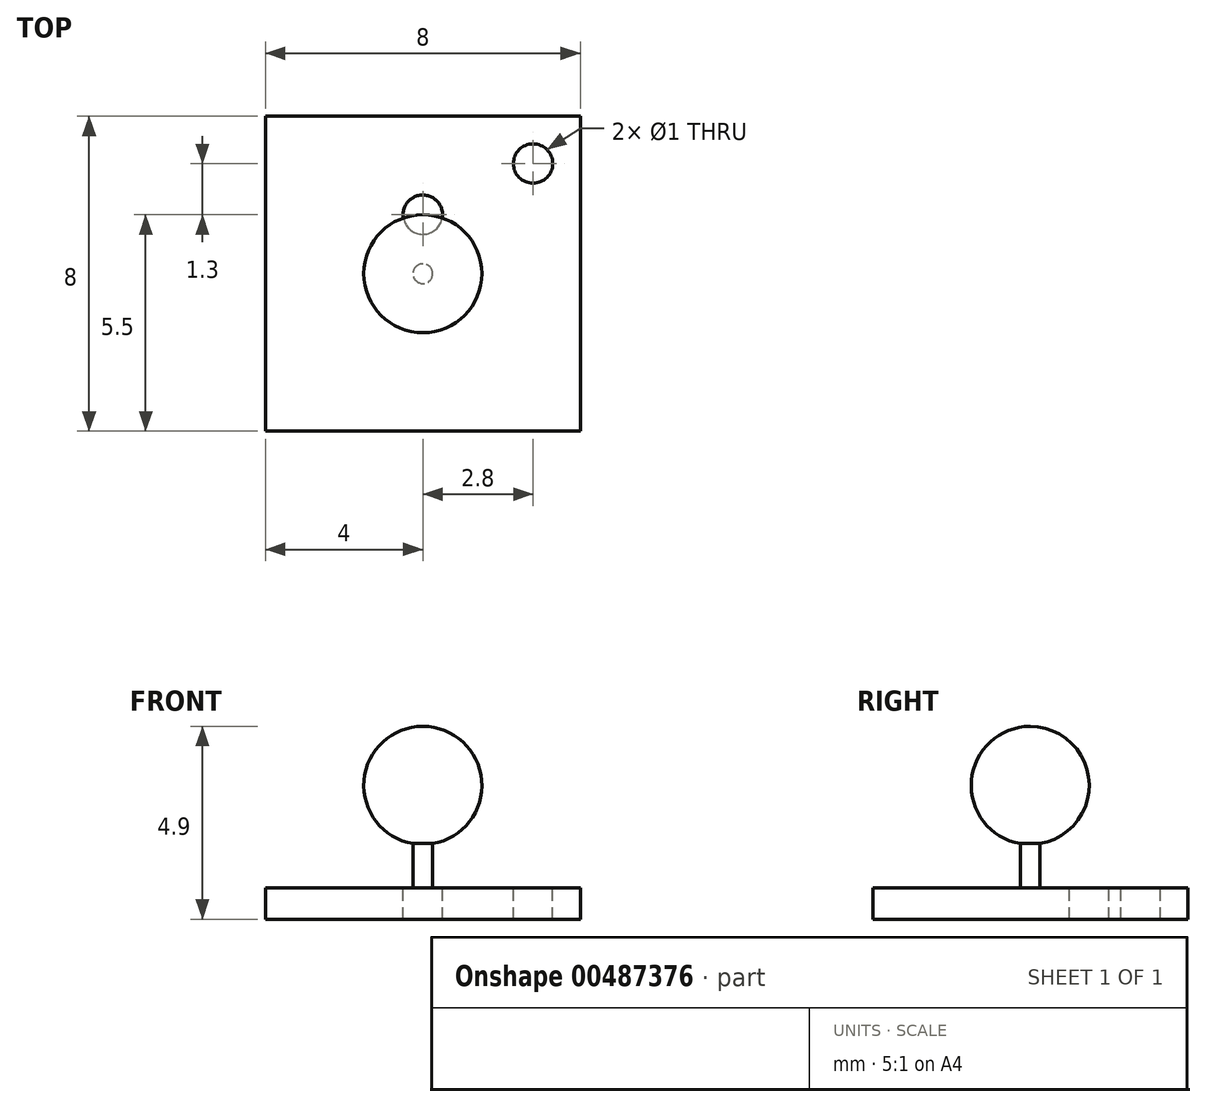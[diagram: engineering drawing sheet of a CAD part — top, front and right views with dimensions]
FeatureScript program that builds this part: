
annotation { "Feature Type Name" : "Feature", "Feature Type Description" : "" }
export const myFeature = defineFeature(function(context is Context, id is Id, definition is map)
    precondition{}
    {
        {
            var Q0;
            Q0=qCreatedBy(makeId("Right.planeOp"),FACE);
            var sketch = newSketch(context, id + "F0", { "sketchPlane" : qUnion([Q0])});
            skLineSegment(sketch, "E0", {"start": v(-0.25, 0) * mm, "end": v(-0.25, 1.12) * mm});
            skLineSegment(sketch, "E1", {"start": v(0, 1.6) * mm, "end": v(0, 0) * mm});
            skLineSegment(sketch, "E2", {"start": v(0, 0) * mm, "end": v(-0.25, 0) * mm});
            skArc(sketch, "E3", {"start": v(0, 4.1) * mm, "mid": v(-1.5, 2.6) * mm, "end": v(0, 1.1) * mm});
            skLineSegment(sketch, "E4", {"start": v(0, 4.1) * mm, "end": v(0, 1.6) * mm});
            skSolve(sketch);
        }
        {
            var Q0;
            Q0 = qSketchRegion(id + "F0", true);
            var Q1;
            Q1=sQuery(id+"F0.wireOp",EDGE,"E4");
            revolve(context, id + "F1", {"entities" : qUnion([Q0]), "axis" : qUnion([Q1]), "revolveType" : RevolveType.FULL});
        }
        {
            var Q0;
            Q0=qCreatedBy(makeId("Top.planeOp"),FACE);
            var sketch = newSketch(context, id + "F2", { "sketchPlane" : qUnion([Q0])});
            skLineSegment(sketch, "E5.bottom", {"start": v(-4, -4) * mm, "end": v(4, -4) * mm});
            skLineSegment(sketch, "E5.top", {"start": v(-4, 4) * mm, "end": v(4, 4) * mm});
            skLineSegment(sketch, "E5.left", {"start": v(-4, -4) * mm, "end": v(-4, 4) * mm});
            skLineSegment(sketch, "E5.right", {"start": v(4, -4) * mm, "end": v(4, 4) * mm});
            skCircle(sketch, "E6", {"center": v(0, 1.5) * mm, "radius": 0.5 * mm});
            skCircle(sketch, "E7", {"center": v(2.8, 2.8) * mm, "radius": 0.5 * mm});
            skSolve(sketch);
        }
        {
            var Q0;
            Q0 = qSketchRegion(id + "F2", true);
            extrude(context, id + "F3", {"entities" : qUnion([Q0]), "operationType" : NewBodyOperationType.ADD, "oppositeDirection" : true, "depth" : 0.8 * mm});
        }
    });
